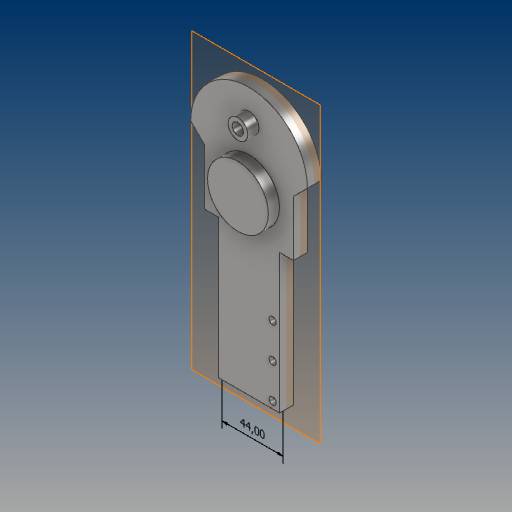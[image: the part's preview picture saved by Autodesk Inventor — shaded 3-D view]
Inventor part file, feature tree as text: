
AUTODESK INVENTOR PART (.ipt)
format: ipt  version: 2021 (Build 250183000, 183)  size: 190,464 bytes
history: native  units: mm
features: other x6, sketch x5, extrude x4, reference x4, projected_geometry x4, plane x1, mirror x1, hole x1
ambient origin geometry x8: Origin, YZ Plane, XZ Plane, XY Plane, X Axis, Y Axis, Z Axis, Center Point
bodies: Solid1 (feature_tree)
feature tree (26):
  other  "Annotations"
  extrude  "Extrusion1"  Depth=7.2mm
  extrude  "Extrusion2"  Depth=43.8mm
  extrude  "Extrusion3"  Depth=42.0mm
  extrude  "Extrusion4"  Depth=8.0mm TaperAngle=0.0deg
  plane  "Work Plane1"
  mirror  "Mirror1"
  hole  "Hole1"  [1 undecoded]
  sketch  "Sketch1"  dims[d0=14.2mm d1=7.2mm]
  reference  "Reference1"
  sketch  "Sketch2"  dims[d2=27.0mm d3=43.8mm]
  projected_geometry  "Projected Loop1"
  projected_geometry  "Projected Loop2"
  sketch  "Sketch3"  dims[d4=42.0mm d5=150.0mm]
  projected_geometry  "Projected Loop3"
  sketch  "Sketch4"  dims[d6=20.0mm d7=8.0mm d8=0.0mm]
  projected_geometry  "Projected Loop4"
  sketch  "Sketch5"  dims[d9=10.0mm d10=0.0mm d11=8.2mm d12=6.0mm d13=4.0mm d14=2.0mm d15=90.0deg d16=8.0mm d17=20.594885mm d18=10.0mm d19=135.0deg d20=10.0mm d21=0.0mm d22=10.0mm d23=100.0mm d27=0.0mm d28=0.0mm d24=0.49838mm d25=7.520724mm d26=44.0mm d29=0.5mm d30=0.872665mm d31=0.5mm d32=0.872665mm]
  reference  "Reference2"
  reference  "Reference3"
  reference  "Reference4"
  other  "<userpath>\Desktop\DO_AN_TOT_NGHIEP_2024\Mechanical\Design_in_3D\Version_1\002_Bo_truot.iam"
  other  "002_Bo_truot.iam"
  other  "16_Khau_hai:1"
  other  "18_Kep_han_A:1"
  other  "Linear Dimension 1"
note: 1 required parameter value undecoded (feature->parameter linkage not recoverable at this tier; creation-order binding heuristic only, values carry confidence <= 0.55)
